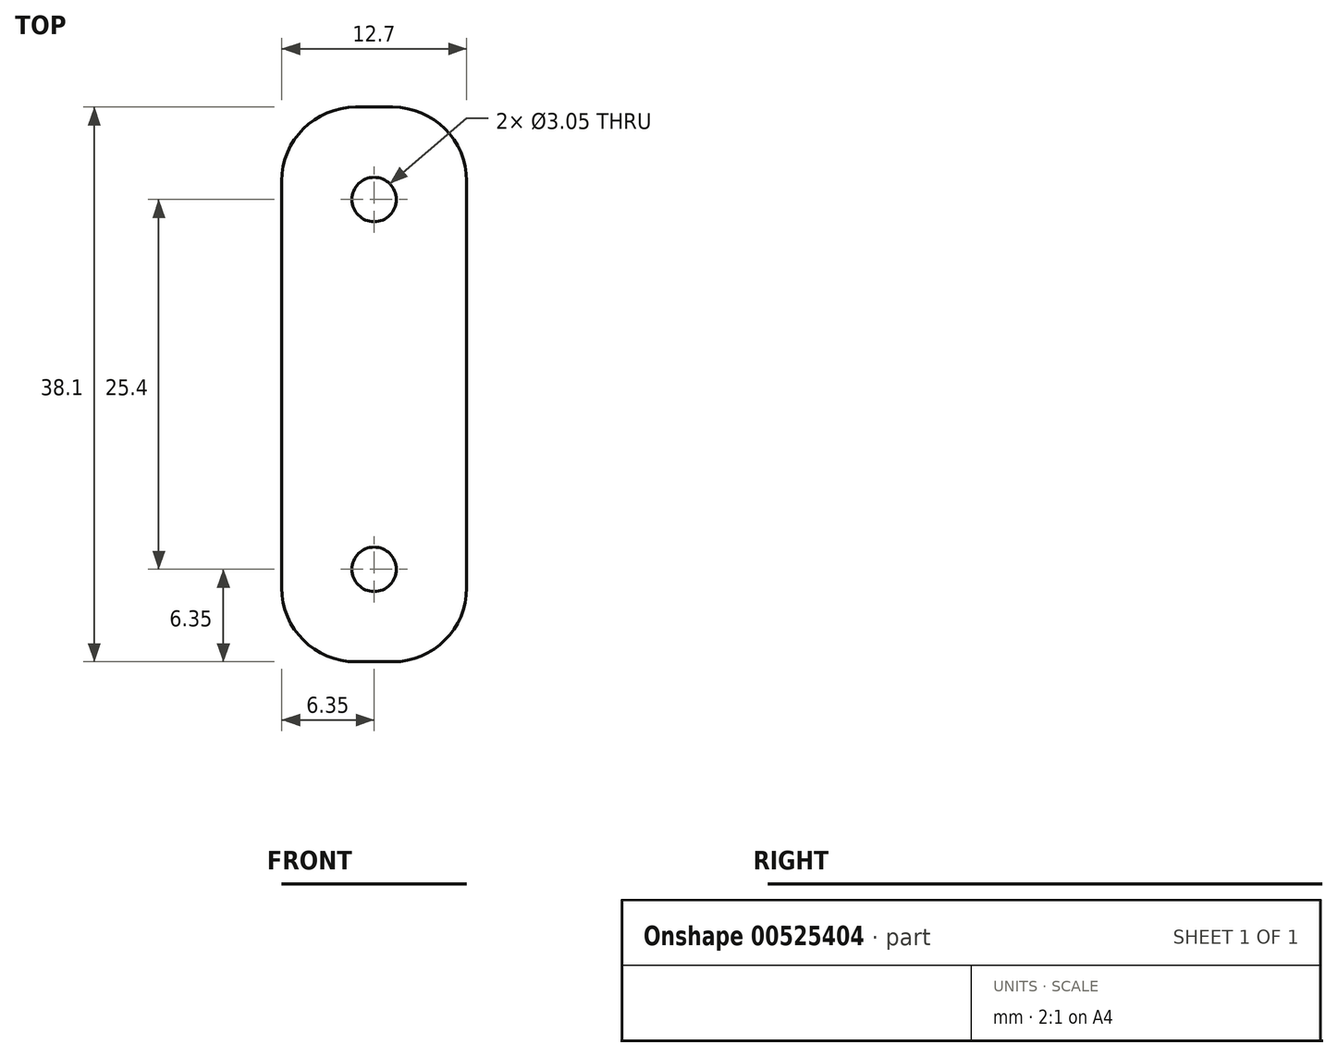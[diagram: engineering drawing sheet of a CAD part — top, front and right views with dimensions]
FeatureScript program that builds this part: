
annotation { "Feature Type Name" : "Feature", "Feature Type Description" : "" }
export const myFeature = defineFeature(function(context is Context, id is Id, definition is map)
    precondition{}
    {
        {
            var Q0;
            Q0=qCreatedBy(makeId("Top.planeOp"),FACE);
            var sketch = newSketch(context, id + "F0", { "sketchPlane" : qUnion([Q0])});
            skLineSegment(sketch, "E0.bottom", {"start": v(6.35, -19.05) * mm, "end": v(-6.35, -19.05) * mm});
            skLineSegment(sketch, "E0.top", {"start": v(6.35, 19.05) * mm, "end": v(-6.35, 19.05) * mm});
            skLineSegment(sketch, "E0.left", {"start": v(6.35, -19.05) * mm, "end": v(6.35, 19.05) * mm});
            skLineSegment(sketch, "E0.right", {"start": v(-6.35, -19.05) * mm, "end": v(-6.35, 19.05) * mm});
            skPoint(sketch, "E0.middle", {"position": v(0, 0) * mm});
            skCircle(sketch, "E1", {"center": v(0, -12.7) * mm, "radius": 1.52 * mm});
            skCircle(sketch, "E2.MirrorC", {"center": v(0, 12.7) * mm, "radius": 1.52 * mm});
            skSolve(sketch);
        }
        {
            var Q0;
            Q0=makeQuery(id+"F0.imprint","IMPRINT",FACE,{"disambiguationData":[TD([[makeQuery(id+"F0.imprint","IMPRINT",EDGE,{"derivedFrom":sQuery(id+"F0.wireOp",EDGE,"E0.bottom")}),-1.0]])]});
            extrude(context, id + "F1", {"entities" : qUnion([Q0]), "depth" : 1 / 203.2 * mm, "offsetDistance" : 25.4 * mm});
        }
        {
            var Q0;
            Q0=makeQuery(id+"F1.opExtrude","SWEPT_EDGE",EDGE,{"disambiguationData":[OSD([sQuery(id+"F0.wireOp",EDGE,"E0.top"),sQuery(id+"F0.wireOp",EDGE,"E0.right")])]});
            var Q1;
            Q1=makeQuery(id+"F1.opExtrude","SWEPT_EDGE",EDGE,{"disambiguationData":[OSD([sQuery(id+"F0.wireOp",EDGE,"E0.top"),sQuery(id+"F0.wireOp",EDGE,"E0.left")])]});
            var Q2;
            Q2=makeQuery(id+"F1.opExtrude","SWEPT_EDGE",EDGE,{"disambiguationData":[OSD([sQuery(id+"F0.wireOp",EDGE,"E0.bottom"),sQuery(id+"F0.wireOp",EDGE,"E0.right")])]});
            var Q3;
            Q3=makeQuery(id+"F1.opExtrude","SWEPT_EDGE",EDGE,{"disambiguationData":[OSD([sQuery(id+"F0.wireOp",EDGE,"E0.bottom"),sQuery(id+"F0.wireOp",EDGE,"E0.left")])]});
            fillet(context, id + "F2", {"entities" : qUnion([Q0, Q1, Q2, Q3]), "radius" : 5.08 * mm, "tangentPropagation" : true, "allowEdgeOverflow" : false});
        }
    });
